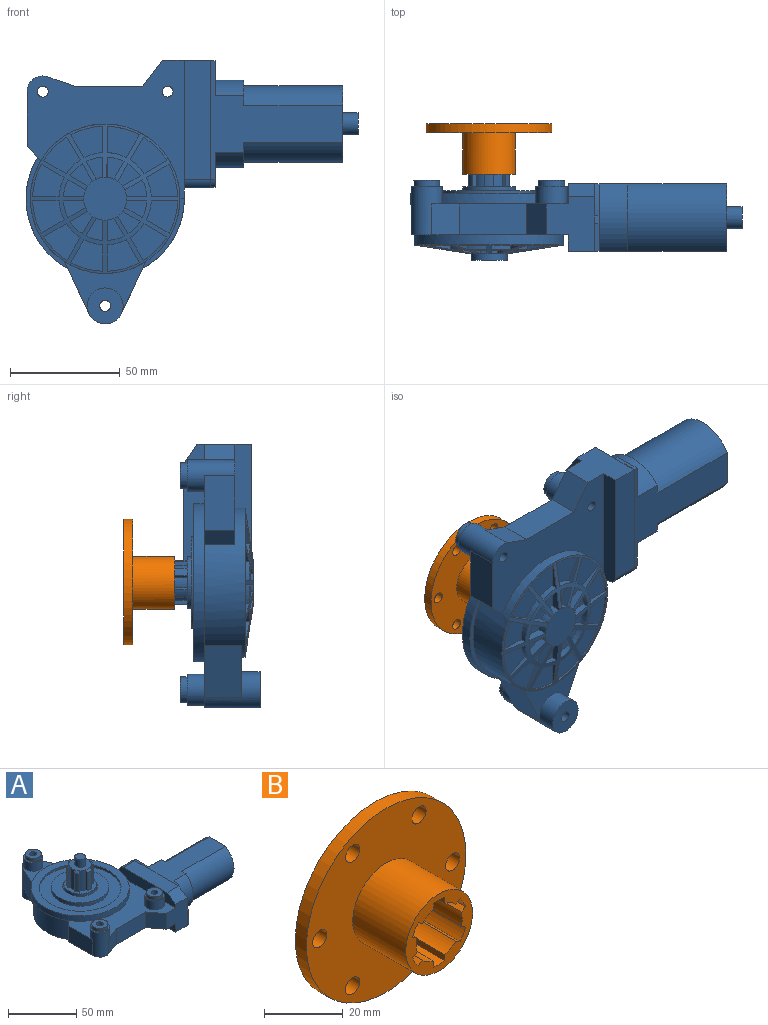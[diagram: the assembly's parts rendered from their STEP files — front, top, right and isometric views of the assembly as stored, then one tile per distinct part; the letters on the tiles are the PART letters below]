
ASSEMBLY  parts=2 mates=1
PART A: 228 faces, bbox 151.2x120.1x58.1 mm
  f0: plane 23.8x23.8mm, normal (0,0,1), area 191.3mm2, adj f114,f115,f116,f117,f118,f119,f120,f121
  f1: plane 58x31mm, normal (1,0,0), area 130.8mm2, adj f11,f86,f88,f90,f91,f92,f93,f94
  f2: plane 71.48x63mm, normal (0,0,-1), area 1956.4mm2, adj f4,f10,f11,f12,f13,f14,f15,f16
  f3: plane 71.48x63mm, normal (0,0,1), area 1497.3mm2, adj f4,f9,f10,f11,f12,f13,f14,f15
  f4: plane 14x5mm, normal (1,0,0), area 70mm2, adj f2,f3,f85,f86
  f5: plane 31.74x19.01mm, normal (0,0,-1), area 72.8mm2, adj f7,f9,f56,f85
  f6: plane 23.67x17mm, normal (-0.91,0.43,0), area 444.6mm2, adj f8,f56,f82,f83,f84
  f7: plane 23.67x17mm, normal (0.91,0.43,0), area 444.6mm2, adj f5,f8,f56,f83,f84
  f8: cylinder r=8.15mm len=25.4mm, axis (0,0,-1), area 743.7mm2, adj f6,f7,f83,f84,f100
  f9: cylinder r=36mm len=72mm, axis (0,0,-1), area 1085.7mm2, adj f3,f5,f57,f82,f83
  f10: plane 14x6.29mm, normal (-0.71,0.71,0), area 124.5mm2, adj f2,f3,f15,f56,f82
  f11: plane 25x22mm, normal (0,-1,0), area 440mm2, adj f1,f2,f3,f14,f87,f89,f90,f223
  f12: plane 14x12.46mm, normal (0.33,-0.94,0), area 184.8mm2, adj f2,f3,f13,f16
  f13: plane 30.5x14mm, normal (0,-1,0), area 427mm2, adj f2,f3,f12,f14
  f14: plane 14x11.94mm, normal (-0.8,-0.6,0), area 210mm2, adj f2,f3,f11,f13
  f15: plane 25x14mm, normal (-1,0,0), area 350mm2, adj f2,f3,f10,f16
  f16: cylinder r=7.1mm len=21.8mm, axis (0,0,-1), area 537.6mm2, adj f2,f3,f12,f15,f101
  f17: cylinder r=9.8mm len=4.5mm, axis (0,0,1), area 14.1mm2, adj f18,f19,f53,f59
  f18: plane 7.99x4.61mm, normal (-0.5,0.87,0), area 34.9mm2, adj f17,f54,f58,f59
  f19: plane 7.99x4.61mm, normal (0.87,-0.5,0), area 34.9mm2, adj f17,f54,f58,f59
  f20: cylinder r=9.8mm len=4.5mm, axis (0,0,1), area 14.1mm2, adj f21,f22,f53,f61
  f21: plane 9.23x4.5mm, normal (0,1,0), area 34.9mm2, adj f20,f54,f60,f61
  f22: plane 7.99x4.61mm, normal (0.5,-0.87,0), area 34.9mm2, adj f20,f54,f60,f61
  f23: cylinder r=9.8mm len=4.5mm, axis (0,0,1), area 14.1mm2, adj f24,f25,f53,f63
  f24: plane 7.99x4.61mm, normal (0.5,0.87,0), area 34.9mm2, adj f23,f54,f62,f63
  f25: plane 9.23x4.5mm, normal (0,-1,0), area 34.9mm2, adj f23,f54,f62,f63
  f26: cylinder r=9.8mm len=4.5mm, axis (0,0,1), area 14.1mm2, adj f27,f28,f53,f65
  f27: plane 7.99x4.61mm, normal (0.87,0.5,0), area 34.9mm2, adj f26,f54,f64,f65
  f28: plane 7.99x4.61mm, normal (-0.5,-0.87,0), area 34.9mm2, adj f26,f54,f64,f65
  f29: cylinder r=9.8mm len=4.5mm, axis (0,0,1), area 14.1mm2, adj f30,f31,f53,f67
  f30: plane 9.45x4.73mm, normal (1,0,0), area 34.9mm2, adj f29,f55,f66,f67
  f31: plane 7.99x4.61mm, normal (-0.87,-0.5,0), area 34.9mm2, adj f29,f54,f66,f67
  f32: cylinder r=9.8mm len=4.5mm, axis (0,0,1), area 14.1mm2, adj f33,f34,f53,f69
  f33: plane 7.99x4.61mm, normal (0.87,-0.5,0), area 34.9mm2, adj f32,f54,f68,f69
  f34: plane 9.23x4.5mm, normal (-1,0,0), area 34.9mm2, adj f32,f54,f68,f69
  f35: cylinder r=9.8mm len=4.5mm, axis (0,0,1), area 14.1mm2, adj f36,f37,f53,f71
  f36: plane 7.99x4.61mm, normal (0.5,-0.87,0), area 34.9mm2, adj f35,f54,f70,f71
  f37: plane 7.99x4.61mm, normal (-0.87,0.5,0), area 34.9mm2, adj f35,f54,f70,f71
  f38: cylinder r=9.8mm len=4.5mm, axis (0,0,1), area 14.1mm2, adj f39,f40,f53,f73
  f39: plane 9.23x4.5mm, normal (0,-1,0), area 34.9mm2, adj f38,f54,f72,f73
  f40: plane 7.99x4.61mm, normal (-0.5,0.87,0), area 34.9mm2, adj f38,f54,f72,f73
  f41: cylinder r=9.8mm len=4.5mm, axis (0,0,1), area 14.1mm2, adj f42,f43,f53,f75
  f42: plane 7.99x4.61mm, normal (-0.5,-0.87,0), area 34.9mm2, adj f41,f54,f74,f75
  f43: plane 9.23x4.5mm, normal (0,1,0), area 34.9mm2, adj f41,f54,f74,f75
  f44: cylinder r=9.8mm len=4.5mm, axis (0,0,1), area 14.1mm2, adj f45,f46,f53,f77
  f45: plane 7.99x4.61mm, normal (-0.87,-0.5,0), area 34.9mm2, adj f44,f54,f76,f77
  f46: plane 7.99x4.61mm, normal (0.5,0.87,0), area 34.9mm2, adj f44,f54,f76,f77
  f47: cylinder r=9.8mm len=4.5mm, axis (0,0,1), area 14.1mm2, adj f48,f49,f53,f79
  f48: plane 9.23x4.5mm, normal (-1,0,0), area 34.9mm2, adj f47,f54,f78,f79
  f49: plane 7.99x4.61mm, normal (0.87,0.5,0), area 34.9mm2, adj f47,f54,f78,f79
  f50: cylinder r=9.8mm len=4.5mm, axis (0,0,1), area 14.1mm2, adj f51,f52,f53,f81
  f51: plane 7.99x4.61mm, normal (-0.87,0.5,0), area 34.9mm2, adj f50,f54,f80,f81
  f52: plane 9.23x4.5mm, normal (1,0,0), area 34.9mm2, adj f50,f54,f80,f81
  f53: plane 19.6x19.6mm, normal (0,0,-1), area 301.7mm2, adj f17,f20,f23,f26,f29,f32,f35,f38
  f54: cone r=34mm half-angle=81.1deg, axis (0,0,1), area 990.6mm2, adj f18,f19,f21,f22,f24,f25,f27,f28
  f55: cone r=34mm half-angle=81.1deg, axis (0,0,1), area 3mm2, adj f30,f53,f54
  f56: cylinder r=34mm len=68mm, axis (0,0,-1), area 2069.3mm2, adj f2,f5,f6,f7,f10,f54,f82,f84
  f57: plane 72x72mm, normal (0,0,1), area 1244.1mm2, adj f9,f109
  f58: cylinder r=19mm len=5.58mm, axis (0,0,-1), area 24.3mm2, adj f18,f19,f54,f59
  f59: plane 10.19x10.19mm, normal (0,0,-1), area 50.9mm2, adj f17,f18,f19,f58
  f60: cylinder r=19mm len=7.62mm, axis (0,0,-1), area 24.3mm2, adj f21,f22,f54,f61
  f61: plane 10.03x7.62mm, normal (0,0,-1), area 50.9mm2, adj f20,f21,f22,f60
  f62: cylinder r=19mm len=7.62mm, axis (0,0,-1), area 24.3mm2, adj f24,f25,f54,f63
  f63: plane 10.03x7.62mm, normal (0,0,-1), area 50.9mm2, adj f23,f24,f25,f62
  f64: cylinder r=19mm len=5.58mm, axis (0,0,-1), area 24.3mm2, adj f27,f28,f54,f65
  f65: plane 10.19x10.19mm, normal (0,0,-1), area 50.9mm2, adj f26,f27,f28,f64
  f66: cylinder r=19mm len=7.62mm, axis (0,0,-1), area 24.3mm2, adj f30,f31,f54,f67
  f67: plane 10.03x7.62mm, normal (0,0,-1), area 50.9mm2, adj f29,f30,f31,f66
  f68: cylinder r=19mm len=7.62mm, axis (0,0,-1), area 24.3mm2, adj f33,f34,f54,f69
  f69: plane 10.03x7.62mm, normal (0,0,-1), area 50.9mm2, adj f32,f33,f34,f68
  f70: cylinder r=19mm len=5.58mm, axis (0,0,-1), area 24.3mm2, adj f36,f37,f54,f71
  f71: plane 10.19x10.19mm, normal (0,0,-1), area 50.9mm2, adj f35,f36,f37,f70
  f72: cylinder r=19mm len=7.62mm, axis (0,0,-1), area 24.3mm2, adj f39,f40,f54,f73
  f73: plane 10.03x7.62mm, normal (0,0,-1), area 50.9mm2, adj f38,f39,f40,f72
  f74: cylinder r=19mm len=7.62mm, axis (0,0,-1), area 24.3mm2, adj f42,f43,f54,f75
  f75: plane 10.03x7.62mm, normal (0,0,-1), area 50.9mm2, adj f41,f42,f43,f74
  f76: cylinder r=19mm len=5.58mm, axis (0,0,-1), area 24.3mm2, adj f45,f46,f54,f77
  f77: plane 10.19x10.19mm, normal (0,0,-1), area 50.9mm2, adj f44,f45,f46,f76
  f78: cylinder r=19mm len=7.62mm, axis (0,0,-1), area 24.3mm2, adj f48,f49,f54,f79
  f79: plane 10.03x7.62mm, normal (0,0,-1), area 50.9mm2, adj f47,f48,f49,f78
  f80: cylinder r=19mm len=7.62mm, axis (0,0,-1), area 24.3mm2, adj f51,f52,f54,f81
  f81: plane 10.03x7.62mm, normal (0,0,-1), area 50.9mm2, adj f50,f51,f52,f80
  f82: plane 50.63x19.01mm, normal (0,0,-1), area 111mm2, adj f6,f9,f10,f56
  f83: plane 33.98x25.14mm, normal (0,0,1), area 291.9mm2, adj f6,f7,f8,f9,f142
  f84: plane 37x23.67mm, normal (0,0,-1), area 315.9mm2, adj f6,f7,f8,f56
  f85: plane 14x2mm, normal (0,1,0), area 28mm2, adj f2,f4,f5,f56
  f86: plane 23.5x12mm, normal (0,1,0), area 282mm2, adj f1,f4,f87,f89,f226,f227
  f87: plane 58x9.3mm, normal (-1,0,0), area 509.4mm2, adj f3,f11,f86,f88,f223,f227
  f88: plane 45.25x12mm, normal (0,0,1), area 543mm2, adj f1,f87,f223,f227
  f89: plane 58x7.7mm, normal (-1,0,0), area 443.6mm2, adj f2,f11,f86,f90,f226
  f90: plane 54.25x12mm, normal (0,0,-1), area 651mm2, adj f1,f11,f89,f226
  f91: plane 12.43x2mm, normal (0,-1,0), area 24.9mm2, adj f1,f92,f96,f97
  f92: plane 60x54.05mm, normal (0,0,-1), area 1196.2mm2, adj f1,f91,f97,f98,f99,f102,f103,f104
  f93: plane 23.5x2mm, normal (0,1,0), area 47mm2, adj f1,f107,f224,f225
  f94: plane 60x42.36mm, normal (0,0,1), area 1172.8mm2, adj f1,f95,f97,f98,f99,f102,f103,f104
  f95: cylinder r=22.95mm len=14.25mm, axis (-1,0,0), area 31.4mm2, adj f1,f94,f96,f97
  f96: plane 5.87x3.92mm, normal (0,-0.55,0.83), area 14.1mm2, adj f1,f91,f95,f97
  f97: plane 30.6x16mm, normal (1,0,0), area 214.6mm2, adj f91,f92,f94,f95,f96,f98
  f98: cylinder r=19.95mm len=30.6mm, axis (-1,0,0), area 453.4mm2, adj f92,f94,f97,f103
  f99: plane 34.9x30.6mm, normal (1,0,0), area 829.3mm2, adj f92,f94,f102,f104,f140
  f100: plane 16.3x16.3mm, normal (0,0,-1), area 189mm2, adj f8,f216
  f101: plane 14.2x14.2mm, normal (0,0,1), area 47.1mm2, adj f16,f146
  f102: cylinder r=17.45mm len=45mm, axis (1,0,0), area 1679.1mm2, adj f92,f94,f99,f103
  f103: plane 30.6x11.56mm, normal (1,0,0), area 89.8mm2, adj f92,f94,f98,f102
  f104: cylinder r=17.45mm len=45mm, axis (1,0,0), area 1679.1mm2, adj f92,f94,f99,f105
  f105: plane 30.6x11.56mm, normal (1,0,0), area 89.8mm2, adj f92,f94,f104,f106
  f106: cylinder r=19.95mm len=30.6mm, axis (1,0,0), area 453.4mm2, adj f92,f94,f105,f107
  f107: plane 30.6x16mm, normal (1,0,0), area 332.1mm2, adj f92,f93,f94,f106,f224,f225
  f108: plane 60x60mm, normal (0,0,1), area 1442mm2, adj f109,f110
  f109: cylinder r=30mm len=60mm, axis (0,0,1), area 358.1mm2, adj f57,f108
  f110: cylinder r=21mm len=42mm, axis (0,0,-1), area 409mm2, adj f108,f111
  f111: plane 42x42mm, normal (0,0,1), area 862.6mm2, adj f110,f113
  f112: plane 25.8x25.8mm, normal (0,0,1), area 77.9mm2, adj f113,f114
  f113: cylinder r=12.9mm len=25.8mm, axis (0,0,1), area 97.3mm2, adj f111,f112
  f114: cylinder r=11.9mm len=23.8mm, axis (0,0,-1), area 224.3mm2, adj f0,f112
  f115: cylinder r=8.2mm len=18mm, axis (0,0,-1), area 81.8mm2, adj f0,f116,f138,f139
  f116: plane 18.04x1.83mm, normal (1,0,0), area 30.7mm2, adj f0,f115,f117,f221
  f117: cylinder r=9.95mm len=16.25mm, axis (0,0,-1), area 65.4mm2, adj f0,f116,f118,f221
  f118: plane 18.04x1.83mm, normal (-1,0,0), area 30.7mm2, adj f0,f117,f119,f221
  f119: cylinder r=8.2mm len=18mm, axis (0,0,-1), area 81.8mm2, adj f0,f118,f120,f139
  f120: plane 18.04x1.59mm, normal (0.5,0.87,0), area 30.7mm2, adj f0,f119,f121,f219
  f121: cylinder r=9.95mm len=16.25mm, axis (0,0,-1), area 65.4mm2, adj f0,f120,f122,f219
  f122: plane 18.04x1.59mm, normal (-0.5,-0.87,0), area 30.7mm2, adj f0,f121,f123,f219
  f123: cylinder r=8.2mm len=18mm, axis (0,0,-1), area 81.8mm2, adj f0,f122,f124,f139
  f124: plane 18.04x1.59mm, normal (-0.5,0.87,0), area 30.7mm2, adj f0,f123,f125,f218
  f125: cylinder r=9.95mm len=16.25mm, axis (0,0,-1), area 65.4mm2, adj f0,f124,f126,f218
  f126: plane 18.04x1.59mm, normal (0.5,-0.87,0), area 30.7mm2, adj f0,f125,f127,f218
  f127: cylinder r=8.2mm len=18mm, axis (0,0,-1), area 81.8mm2, adj f0,f126,f128,f139
  f128: plane 18.04x1.83mm, normal (-1,0,0), area 30.7mm2, adj f0,f127,f129,f217
  f129: cylinder r=9.95mm len=16.25mm, axis (0,0,-1), area 65.4mm2, adj f0,f128,f130,f217
  f130: plane 18.04x1.83mm, normal (1,0,0), area 30.7mm2, adj f0,f129,f131,f217
  f131: cylinder r=8.2mm len=18mm, axis (0,0,-1), area 81.8mm2, adj f0,f130,f132,f139
  f132: plane 18.04x1.59mm, normal (-0.5,-0.87,0), area 30.7mm2, adj f0,f131,f133,f220
  f133: cylinder r=9.95mm len=16.25mm, axis (0,0,-1), area 65.4mm2, adj f0,f132,f134,f220
  f134: plane 18.04x1.59mm, normal (0.5,0.87,0), area 30.7mm2, adj f0,f133,f135,f220
  f135: cylinder r=8.2mm len=18mm, axis (0,0,-1), area 81.8mm2, adj f0,f134,f136,f139
  f136: plane 18.04x1.59mm, normal (0.5,-0.87,0), area 30.7mm2, adj f0,f135,f137,f222
  f137: cylinder r=9.95mm len=16.25mm, axis (0,0,-1), area 65.4mm2, adj f0,f136,f138,f222
  f138: plane 18.04x1.59mm, normal (-0.5,0.87,0), area 30.7mm2, adj f0,f115,f137,f222
  f139: plane 16.4x16.4mm, normal (0,0,1), area 161mm2, adj f115,f119,f123,f127,f131,f135,f212,f217
  f140: cylinder r=5mm len=10mm, axis (-1,0,0), area 219.9mm2, adj f99,f141
  f141: plane 10x10mm, normal (1,0,0), area 78.5mm2, adj f140
  f142: cylinder r=7.1mm len=14.2mm, axis (0,0,-1), area 348mm2, adj f83,f143
  f143: plane 14.2x14.2mm, normal (0,0,1), area 47.1mm2, adj f142,f144
  f144: cylinder r=5.95mm len=11.9mm, axis (0,0,-1), area 112.2mm2, adj f143,f145
  f145: plane 11.9x11.9mm, normal (0,0,1), area 91.6mm2, adj f144,f216
  f146: cylinder r=5.95mm len=11.9mm, axis (0,0,-1), area 112.2mm2, adj f101,f147
  f147: plane 11.9x11.9mm, normal (0,0,1), area 91.6mm2, adj f146,f215
  f148: cylinder r=7.1mm len=14.2mm, axis (0,0,-1), area 348mm2, adj f3,f149
  f149: plane 14.2x14.2mm, normal (0,0,1), area 47.1mm2, adj f148,f150
  f150: cylinder r=5.95mm len=11.9mm, axis (0,0,-1), area 112.2mm2, adj f149,f151
  f151: plane 11.9x11.9mm, normal (0,0,1), area 91.6mm2, adj f150,f214
  f152: cylinder r=33mm len=14.63mm, axis (0,0,1), area 13.1mm2, adj f54,f153,f155,f156
  f153: plane 10.5x6.11mm, normal (-0.87,0.5,0), area 21.6mm2, adj f54,f152,f154,f156
  f154: cylinder r=21mm len=8.62mm, axis (0,0,1), area 24.7mm2, adj f54,f153,f155,f156
  f155: plane 12.11x2.85mm, normal (1,0,0), area 21.6mm2, adj f54,f152,f154,f156
  f156: plane 14.63x14.32mm, normal (0,0,-1), area 145.6mm2, adj f152,f153,f154,f155
  f157: cylinder r=33mm len=10.71mm, axis (0,0,1), area 13.1mm2, adj f54,f158,f160,f161
  f158: plane 10.5x6.11mm, normal (-0.5,0.87,0), area 21.6mm2, adj f54,f157,f159,f161
  f159: cylinder r=21mm len=6.31mm, axis (0,0,1), area 24.7mm2, adj f54,f158,f160,f161
  f160: plane 10.5x6.11mm, normal (0.87,-0.5,0), area 21.6mm2, adj f54,f157,f159,f161
  f161: plane 16.71x16.71mm, normal (0,0,-1), area 145.6mm2, adj f157,f158,f159,f160
  f162: cylinder r=33mm len=14.63mm, axis (0,0,1), area 13.1mm2, adj f54,f163,f165,f166
  f163: plane 12.11x2.85mm, normal (0,1,0), area 21.6mm2, adj f54,f162,f164,f166
  f164: cylinder r=21mm len=8.62mm, axis (0,0,1), area 24.7mm2, adj f54,f163,f165,f166
  f165: plane 10.5x6.11mm, normal (0.5,-0.87,0), area 21.6mm2, adj f54,f162,f164,f166
  f166: plane 14.63x14.32mm, normal (0,0,-1), area 145.6mm2, adj f162,f163,f164,f165
  f167: cylinder r=33mm len=14.63mm, axis (0,0,1), area 13.1mm2, adj f54,f168,f170,f171
  f168: plane 10.5x6.11mm, normal (0.5,0.87,0), area 21.6mm2, adj f54,f167,f169,f171
  f169: cylinder r=21mm len=8.62mm, axis (0,0,1), area 24.7mm2, adj f54,f168,f170,f171
  f170: plane 12.11x2.85mm, normal (0,-1,0), area 21.6mm2, adj f54,f167,f169,f171
  f171: plane 14.63x14.32mm, normal (0,0,-1), area 145.6mm2, adj f167,f168,f169,f170
  f172: cylinder r=33mm len=10.71mm, axis (0,0,1), area 13.1mm2, adj f54,f173,f175,f176
  f173: plane 10.5x6.11mm, normal (0.87,0.5,0), area 21.6mm2, adj f54,f172,f174,f176
  f174: cylinder r=21mm len=6.31mm, axis (0,0,1), area 24.7mm2, adj f54,f173,f175,f176
  f175: plane 10.5x6.11mm, normal (-0.5,-0.87,0), area 21.6mm2, adj f54,f172,f174,f176
  f176: plane 16.71x16.71mm, normal (0,0,-1), area 145.6mm2, adj f172,f173,f174,f175
  f177: cylinder r=33mm len=14.63mm, axis (0,0,1), area 13.1mm2, adj f54,f178,f180,f181
  f178: plane 12.11x2.85mm, normal (1,0,0), area 21.6mm2, adj f54,f177,f179,f181
  f179: cylinder r=21mm len=8.62mm, axis (0,0,1), area 24.7mm2, adj f54,f178,f180,f181
  f180: plane 10.5x6.11mm, normal (-0.87,-0.5,0), area 21.6mm2, adj f54,f177,f179,f181
  f181: plane 14.63x14.32mm, normal (0,0,-1), area 145.6mm2, adj f177,f178,f179,f180
  f182: cylinder r=33mm len=14.63mm, axis (0,0,1), area 13.1mm2, adj f54,f183,f185,f186
  f183: plane 10.5x6.11mm, normal (0.87,-0.5,0), area 21.6mm2, adj f54,f182,f184,f186
  f184: cylinder r=21mm len=8.62mm, axis (0,0,1), area 24.7mm2, adj f54,f183,f185,f186
  f185: plane 12.11x2.85mm, normal (-1,0,0), area 21.6mm2, adj f54,f182,f184,f186
  f186: plane 14.63x14.32mm, normal (0,0,-1), area 145.6mm2, adj f182,f183,f184,f185
  f187: cylinder r=33mm len=10.71mm, axis (0,0,1), area 13.1mm2, adj f54,f188,f190,f191
  f188: plane 10.5x6.11mm, normal (0.5,-0.87,0), area 21.6mm2, adj f54,f187,f189,f191
  f189: cylinder r=21mm len=6.31mm, axis (0,0,1), area 24.7mm2, adj f54,f188,f190,f191
  f190: plane 10.5x6.11mm, normal (-0.87,0.5,0), area 21.6mm2, adj f54,f187,f189,f191
  f191: plane 16.71x16.71mm, normal (0,0,-1), area 145.6mm2, adj f187,f188,f189,f190
  f192: cylinder r=33mm len=14.63mm, axis (0,0,1), area 13.1mm2, adj f54,f193,f195,f196
  f193: plane 12.11x2.85mm, normal (0,-1,0), area 21.6mm2, adj f54,f192,f194,f196
  f194: cylinder r=21mm len=8.62mm, axis (0,0,1), area 24.7mm2, adj f54,f193,f195,f196
  f195: plane 10.5x6.11mm, normal (-0.5,0.87,0), area 21.6mm2, adj f54,f192,f194,f196
  f196: plane 14.63x14.32mm, normal (0,0,-1), area 145.6mm2, adj f192,f193,f194,f195
  f197: cylinder r=33mm len=14.63mm, axis (0,0,1), area 13.1mm2, adj f54,f198,f200,f201
  f198: plane 10.5x6.11mm, normal (-0.5,-0.87,0), area 21.6mm2, adj f54,f197,f199,f201
  f199: cylinder r=21mm len=8.62mm, axis (0,0,1), area 24.7mm2, adj f54,f198,f200,f201
  f200: plane 12.11x2.85mm, normal (0,1,0), area 21.6mm2, adj f54,f197,f199,f201
  f201: plane 14.63x14.32mm, normal (0,0,-1), area 145.6mm2, adj f197,f198,f199,f200
  f202: cylinder r=33mm len=10.71mm, axis (0,0,1), area 13.1mm2, adj f54,f203,f205,f206
  f203: plane 10.5x6.11mm, normal (-0.87,-0.5,0), area 21.6mm2, adj f54,f202,f204,f206
  f204: cylinder r=21mm len=6.31mm, axis (0,0,1), area 24.7mm2, adj f54,f203,f205,f206
  f205: plane 10.5x6.11mm, normal (0.5,0.87,0), area 21.6mm2, adj f54,f202,f204,f206
  f206: plane 16.71x16.71mm, normal (0,0,-1), area 145.6mm2, adj f202,f203,f204,f205
  f207: cylinder r=33mm len=14.63mm, axis (0,0,1), area 13.1mm2, adj f54,f208,f210,f211
  f208: plane 12.11x2.85mm, normal (-1,0,0), area 21.6mm2, adj f54,f207,f209,f211
  f209: cylinder r=21mm len=8.62mm, axis (0,0,1), area 24.7mm2, adj f54,f208,f210,f211
  f210: plane 10.5x6.11mm, normal (0.87,0.5,0), area 21.6mm2, adj f54,f207,f209,f211
  f211: plane 14.63x14.32mm, normal (0,0,-1), area 145.6mm2, adj f207,f208,f209,f210
  f212: cylinder r=4mm len=8mm, axis (0,0,1), area 168.4mm2, adj f139,f213
  f213: plane 8x8mm, normal (0,0,1), area 50.3mm2, adj f212
  f214: cylinder r=2.5mm len=24.8mm, axis (0,0,-1), area 389.6mm2, adj f2,f151
  f215: cylinder r=2.5mm len=24.8mm, axis (0,0,-1), area 389.6mm2, adj f2,f147
  f216: cylinder r=2.5mm len=36.2mm, axis (0,0,-1), area 568.6mm2, adj f100,f145
  f217: cone r=8.2mm half-angle=45deg, axis (0,0,-1), area 10mm2, adj f128,f129,f130,f139
  f218: cone r=8.2mm half-angle=45deg, axis (0,0,-1), area 10mm2, adj f124,f125,f126,f139
  f219: cone r=8.2mm half-angle=45deg, axis (0,0,-1), area 10mm2, adj f120,f121,f122,f139
  f220: cone r=8.2mm half-angle=45deg, axis (0,0,-1), area 10mm2, adj f132,f133,f134,f139
  f221: cone r=8.2mm half-angle=45deg, axis (0,0,-1), area 10mm2, adj f116,f117,f118,f139
  f222: cone r=8.2mm half-angle=45deg, axis (0,0,-1), area 10mm2, adj f136,f137,f138,f139
  f223: plane 12x9mm, normal (0,-0.55,0.83), area 129.8mm2, adj f1,f11,f87,f88
  f224: cylinder r=3.55mm len=3.55mm, axis (-1,0,0), area 11.2mm2, adj f1,f93,f94,f107
  f225: cylinder r=3.55mm len=3.55mm, axis (-1,0,0), area 11.2mm2, adj f1,f92,f93,f107
  f226: cylinder r=3.75mm len=12mm, axis (1,0,0), area 70.7mm2, adj f1,f86,f89,f90
  f227: cylinder r=3.75mm len=12mm, axis (-1,0,0), area 70.7mm2, adj f1,f86,f87,f88
PART B: 36 faces, bbox 57.2x23x57.2 mm
  f0: plane 19x1.56mm, normal (0.5,0,-0.87), area 34.3mm2, adj f1,f23,f25,f35
  f1: cylinder r=10.02mm len=19mm, axis (0,1,0), area 77mm2, adj f0,f2,f25,f35
  f2: plane 19x1.56mm, normal (-0.5,0,0.87), area 34.3mm2, adj f1,f3,f25,f35
  f3: cylinder r=8.26mm len=19mm, axis (0,1,0), area 87mm2, adj f2,f4,f25,f35
  f4: plane 19x1.56mm, normal (-0.5,0,-0.87), area 34.3mm2, adj f3,f5,f25,f35
  f5: cylinder r=10.02mm len=19mm, axis (0,1,0), area 77mm2, adj f4,f6,f25,f35
  f6: plane 19x1.56mm, normal (0.5,0,0.87), area 34.3mm2, adj f5,f7,f25,f35
  f7: cylinder r=8.26mm len=19mm, axis (0,1,0), area 87mm2, adj f6,f8,f25,f35
  f8: plane 19x1.81mm, normal (-1,0,0), area 34.3mm2, adj f7,f9,f25,f35
  f9: cylinder r=10.02mm len=19mm, axis (0,1,0), area 77mm2, adj f8,f10,f25,f35
  f10: plane 19x1.81mm, normal (1,0,0), area 34.3mm2, adj f9,f11,f25,f35
  f11: cylinder r=8.26mm len=19mm, axis (0,1,0), area 87mm2, adj f10,f12,f25,f35
  f12: plane 19x1.56mm, normal (-0.5,0,0.87), area 34.3mm2, adj f11,f13,f25,f35
  f13: cylinder r=10.02mm len=19mm, axis (0,1,0), area 77mm2, adj f12,f14,f25,f35
  f14: plane 19x1.56mm, normal (0.5,0,-0.87), area 34.3mm2, adj f13,f15,f25,f35
  f15: cylinder r=8.26mm len=19mm, axis (0,1,0), area 87mm2, adj f14,f16,f25,f35
  f16: plane 19x1.56mm, normal (0.5,0,0.87), area 34.3mm2, adj f15,f17,f25,f35
  f17: cylinder r=10.02mm len=19mm, axis (0,1,0), area 77mm2, adj f16,f18,f25,f35
  f18: plane 19x1.56mm, normal (-0.5,0,-0.87), area 34.3mm2, adj f17,f19,f25,f35
  f19: cylinder r=8.26mm len=19mm, axis (0,1,0), area 87mm2, adj f18,f20,f25,f35
  f20: plane 19x1.81mm, normal (1,0,0), area 34.3mm2, adj f19,f21,f25,f35
  f21: cylinder r=10.02mm len=19mm, axis (0,1,0), area 77mm2, adj f20,f22,f25,f35
  f22: plane 19x1.81mm, normal (-1,0,0), area 34.3mm2, adj f21,f23,f25,f35
  f23: cylinder r=8.26mm len=19mm, axis (0,1,0), area 87mm2, adj f0,f22,f25,f35
  f24: cylinder r=11.98mm len=23.96mm, axis (0,1,0), area 1430.3mm2, adj f25,f26
  f25: plane 23.96x23.96mm, normal (0,-1,0), area 193.9mm2, adj f0,f1,f2,f3,f4,f5,f6,f7
  f26: plane 57.15x57.15mm, normal (0,-1,0), area 1992.7mm2, adj f24,f27,f28,f29,f30,f31,f32,f33
  f27: cylinder r=2.54mm len=5.08mm, axis (0,1,0), area 63.8mm2, adj f26,f34
  f28: cylinder r=2.54mm len=5.08mm, axis (0,1,0), area 63.8mm2, adj f26,f34
  f29: cylinder r=2.54mm len=5.08mm, axis (0,1,0), area 63.8mm2, adj f26,f34
  f30: cylinder r=28.57mm len=57.15mm, axis (0,1,0), area 718.2mm2, adj f26,f34
  f31: cylinder r=2.54mm len=5.08mm, axis (0,1,0), area 63.8mm2, adj f26,f34
  f32: cylinder r=2.54mm len=5.08mm, axis (0,1,0), area 63.8mm2, adj f26,f34
  f33: cylinder r=2.54mm len=5.08mm, axis (0,1,0), area 63.8mm2, adj f26,f34
  f34: plane 57.15x57.15mm, normal (0,1,0), area 2443.6mm2, adj f27,f28,f29,f30,f31,f32,f33
  f35: plane 20.04x19.01mm, normal (0,-1,0), area 257mm2, adj f0,f1,f2,f3,f4,f5,f6,f7
PLACE A rot(axis=(-1,0,0),90deg) t=(-169.13,49.31,28.32)mm
PLACE B t=(-169.13,81.01,28.72)mm
MATE fastened A.f9 <-> B.f3  axis (0,1,0) through (-169.13,77.01,28.32)mm
